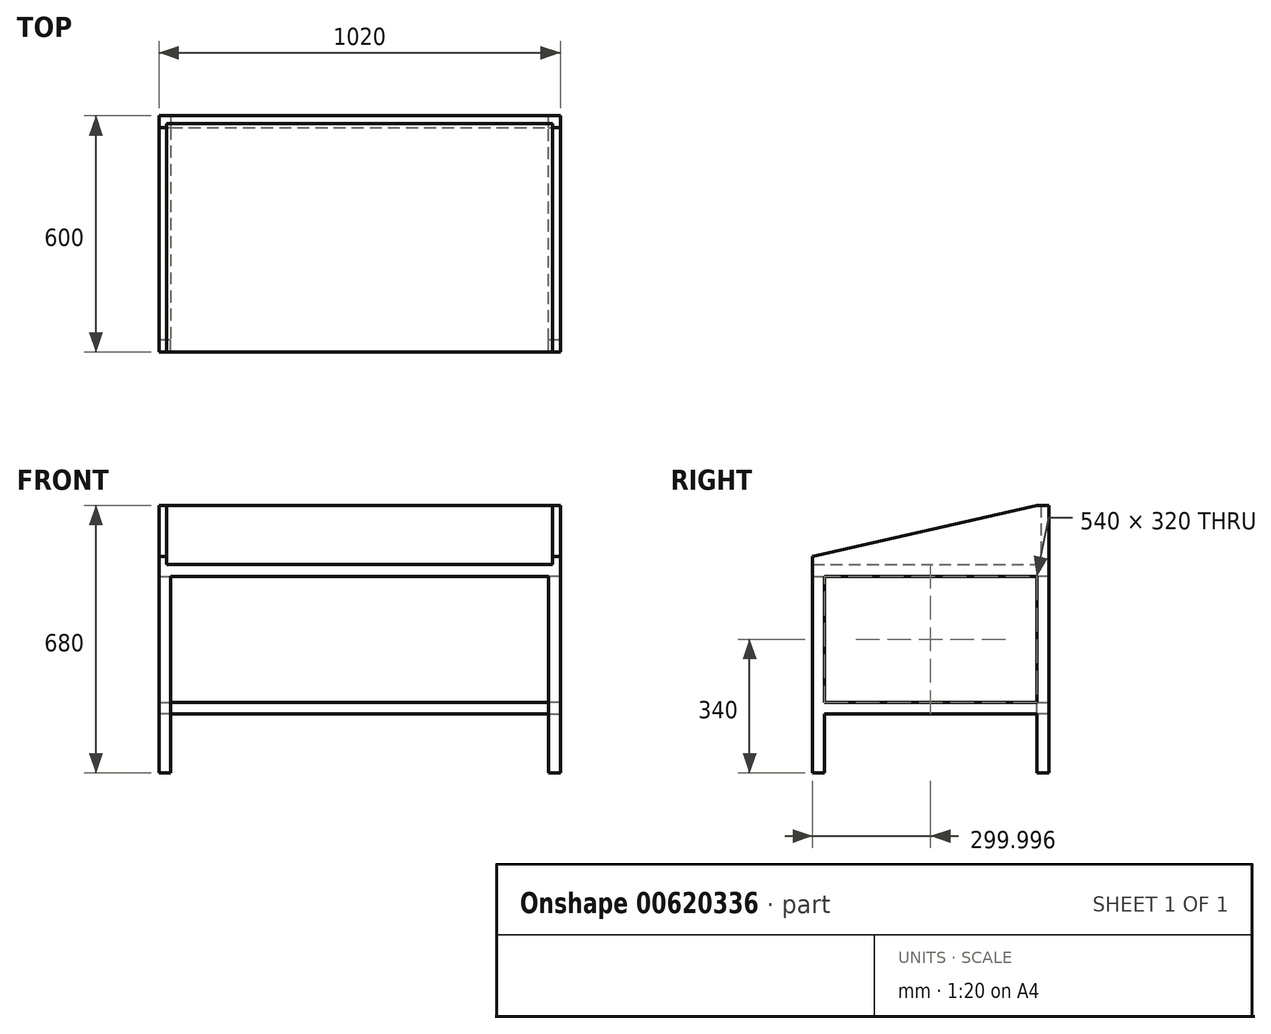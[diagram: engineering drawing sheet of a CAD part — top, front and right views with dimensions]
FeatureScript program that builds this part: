
annotation { "Feature Type Name" : "Feature", "Feature Type Description" : "" }
export const myFeature = defineFeature(function(context is Context, id is Id, definition is map)
    precondition{}
    {
        {
            var Q0;
            Q0=qCreatedBy(makeId("Top.planeOp"),FACE);
            var sketch = newSketch(context, id + "F0", { "sketchPlane" : qUnion([Q0])});
            skLineSegment(sketch, "E0.bottom", {"start": v(-508.02, 248.14) * mm, "end": v(511.98, 248.14) * mm});
            skLineSegment(sketch, "E0.top", {"start": v(-508.02, -351.86) * mm, "end": v(511.98, -351.86) * mm});
            skLineSegment(sketch, "E0.left", {"start": v(-508.02, 248.14) * mm, "end": v(-508.02, -351.86) * mm});
            skLineSegment(sketch, "E0.right", {"start": v(511.98, 248.14) * mm, "end": v(511.98, -351.86) * mm});
            skSolve(sketch);
        }
        {
            var Q0;
            Q0=makeQuery(id+"F0.imprint","IMPRINT",FACE,{"disambiguationData":[TD([[makeQuery(id+"F0.imprint","IMPRINT",EDGE,{"derivedFrom":sQuery(id+"F0.wireOp",EDGE,"E0.bottom")}),-1.0]])]});
            extrude(context, id + "F1", {"entities" : qUnion([Q0]), "depth" : 30 * mm, "offsetDistance" : 25 * mm});
        }
        {
            var Q0;
            Q0=makeQuery(id+"F1.opExtrude","CAP_FACE",FACE,{"disambiguationData":[OSD([sQuery(id+"F0.wireOp",EDGE,"E0.bottom"),sQuery(id+"F0.wireOp",EDGE,"E0.top"),sQuery(id+"F0.wireOp",EDGE,"E0.left"),sQuery(id+"F0.wireOp",EDGE,"E0.right")])],"isStart":false});
            var sketch = newSketch(context, id + "F2", { "sketchPlane" : qUnion([Q0])});
            skLineSegment(sketch, "E1", {"start": v(-508.02, -351.86) * mm, "end": v(-508.02, 248.14) * mm});
            skLineSegment(sketch, "E2", {"start": v(-508.02, 248.14) * mm, "end": v(511.98, 248.14) * mm});
            skLineSegment(sketch, "E3", {"start": v(511.98, 248.14) * mm, "end": v(511.98, -351.86) * mm});
            skLineSegment(sketch, "E4", {"start": v(511.98, -351.86) * mm, "end": v(491.98, -351.86) * mm});
            skLineSegment(sketch, "E5", {"start": v(491.98, -351.86) * mm, "end": v(491.98, 228.14) * mm});
            skLineSegment(sketch, "E6", {"start": v(491.98, 228.14) * mm, "end": v(-488.02, 228.14) * mm});
            skLineSegment(sketch, "E7", {"start": v(-488.02, 228.14) * mm, "end": v(-488.02, -351.86) * mm});
            skLineSegment(sketch, "E8", {"start": v(-488.02, -351.86) * mm, "end": v(-508.02, -351.86) * mm});
            skSolve(sketch);
        }
        {
            var Q0;
            Q0 = qSketchRegion(id + "F2", true);
            extrude(context, id + "F3", {"entities" : qUnion([Q0]), "operationType" : NewBodyOperationType.ADD, "depth" : 150 * mm, "offsetDistance" : 25 * mm});
        }
        {
            var Q0;
            Q0=makeQuery(id+"F3.boolean.opBoolean","MERGE",FACE,{"derivedFrom":[makeQuery(id+"F1.opExtrude","SWEPT_FACE",FACE,{"disambiguationData":[OSD([sQuery(id+"F0.wireOp",EDGE,"E0.left")])]}),makeQuery(id+"F3.opExtrude","SWEPT_FACE",FACE,{"disambiguationData":[OSD([sQuery(id+"F2.wireOp",EDGE,"E1")])]})]});
            var sketch = newSketch(context, id + "F4", { "sketchPlane" : qUnion([Q0])});
            skLineSegment(sketch, "E9", {"start": v(-218.14, 180) * mm, "end": v(351.86, 50) * mm});
            skLineSegment(sketch, "E10", {"start": v(351.86, 50) * mm, "end": v(351.86, 180) * mm});
            skLineSegment(sketch, "E11", {"start": v(351.86, 180) * mm, "end": v(-218.14, 180) * mm});
            skSolve(sketch);
        }
        {
            var Q0;
            Q0=makeQuery(id+"F4.imprint","IMPRINT",FACE,{"disambiguationData":[TD([[makeQuery(id+"F4.imprint","IMPRINT",EDGE,{"derivedFrom":sQuery(id+"F4.wireOp",EDGE,"E9")}),1.0]])]});
            extrude(context, id + "F5", {"entities" : qUnion([Q0]), "operationType" : NewBodyOperationType.REMOVE, "oppositeDirection" : true, "depth" : 2000 * mm, "offsetDistance" : 25 * mm});
        }
        {
            var Q0;
            Q0=makeQuery(id+"F1.opExtrude","CAP_FACE",FACE,{"disambiguationData":[OSD([sQuery(id+"F0.wireOp",EDGE,"E0.bottom"),sQuery(id+"F0.wireOp",EDGE,"E0.top"),sQuery(id+"F0.wireOp",EDGE,"E0.left"),sQuery(id+"F0.wireOp",EDGE,"E0.right")])],"isStart":true});
            var sketch = newSketch(context, id + "F6", { "sketchPlane" : qUnion([Q0])});
            skLineSegment(sketch, "E12.bottom", {"start": v(-508.02, 351.86) * mm, "end": v(-478.02, 351.86) * mm});
            skLineSegment(sketch, "E12.top", {"start": v(-508.02, 321.86) * mm, "end": v(-478.02, 321.86) * mm});
            skLineSegment(sketch, "E12.left", {"start": v(-508.02, 351.86) * mm, "end": v(-508.02, 321.86) * mm});
            skLineSegment(sketch, "E12.right", {"start": v(-478.02, 351.86) * mm, "end": v(-478.02, 321.86) * mm});
            skLineSegment(sketch, "E13.bottom", {"start": v(-508.02, -248.14) * mm, "end": v(-478.02, -248.14) * mm});
            skLineSegment(sketch, "E13.top", {"start": v(-508.02, -218.14) * mm, "end": v(-478.02, -218.14) * mm});
            skLineSegment(sketch, "E13.left", {"start": v(-508.02, -248.14) * mm, "end": v(-508.02, -218.14) * mm});
            skLineSegment(sketch, "E13.right", {"start": v(-478.02, -248.14) * mm, "end": v(-478.02, -218.14) * mm});
            skLineSegment(sketch, "E14.bottom", {"start": v(511.98, 351.86) * mm, "end": v(481.98, 351.86) * mm});
            skLineSegment(sketch, "E14.top", {"start": v(511.98, 321.86) * mm, "end": v(481.98, 321.86) * mm});
            skLineSegment(sketch, "E14.left", {"start": v(511.98, 351.86) * mm, "end": v(511.98, 321.86) * mm});
            skLineSegment(sketch, "E14.right", {"start": v(481.98, 351.86) * mm, "end": v(481.98, 321.86) * mm});
            skLineSegment(sketch, "E15.bottom", {"start": v(511.98, -248.14) * mm, "end": v(481.98, -248.14) * mm});
            skLineSegment(sketch, "E15.top", {"start": v(511.98, -218.14) * mm, "end": v(481.98, -218.14) * mm});
            skLineSegment(sketch, "E15.left", {"start": v(511.98, -248.14) * mm, "end": v(511.98, -218.14) * mm});
            skLineSegment(sketch, "E15.right", {"start": v(481.98, -248.14) * mm, "end": v(481.98, -218.14) * mm});
            skSolve(sketch);
        }
        {
            var Q0;
            Q0 = qSketchRegion(id + "F6", true);
            extrude(context, id + "F7", {"entities" : qUnion([Q0]), "operationType" : NewBodyOperationType.ADD, "depth" : 500 * mm, "offsetDistance" : 25 * mm});
        }
        {
            var Q0;
            Q0=makeQuery(id+"F7.opExtrude","SWEPT_FACE",FACE,{"disambiguationData":[OSD([sQuery(id+"F6.wireOp",EDGE,"E12.top")])]});
            var sketch = newSketch(context, id + "F8", { "sketchPlane" : qUnion([Q0])});
            skLineSegment(sketch, "E16.bottom", {"start": v(478.02, -320) * mm, "end": v(508.02, -320) * mm});
            skLineSegment(sketch, "E16.top", {"start": v(478.02, -350) * mm, "end": v(508.02, -350) * mm});
            skLineSegment(sketch, "E16.left", {"start": v(478.02, -320) * mm, "end": v(478.02, -350) * mm});
            skLineSegment(sketch, "E16.right", {"start": v(508.02, -320) * mm, "end": v(508.02, -350) * mm});
            skSolve(sketch);
        }
        {
            var Q0;
            Q0 = qSketchRegion(id + "F8", true);
            extrude(context, id + "F9", {"entities" : qUnion([Q0]), "operationType" : NewBodyOperationType.ADD, "endBound" : BoundingType.UP_TO_NEXT, "depth" : 25 * mm, "offsetDistance" : 25 * mm});
        }
        {
            var Q0;
            Q0=makeQuery(id+"F7.opExtrude","SWEPT_FACE",FACE,{"disambiguationData":[OSD([sQuery(id+"F6.wireOp",EDGE,"E15.top")])]});
            var sketch = newSketch(context, id + "F10", { "sketchPlane" : qUnion([Q0])});
            skLineSegment(sketch, "E17.bottom", {"start": v(481.98, -320) * mm, "end": v(511.98, -320) * mm});
            skLineSegment(sketch, "E17.top", {"start": v(481.98, -350) * mm, "end": v(511.98, -350) * mm});
            skLineSegment(sketch, "E17.left", {"start": v(481.98, -320) * mm, "end": v(481.98, -350) * mm});
            skLineSegment(sketch, "E17.right", {"start": v(511.98, -320) * mm, "end": v(511.98, -350) * mm});
            skSolve(sketch);
        }
        {
            var Q0;
            Q0 = qSketchRegion(id + "F10", true);
            extrude(context, id + "F11", {"entities" : qUnion([Q0]), "operationType" : NewBodyOperationType.ADD, "endBound" : BoundingType.UP_TO_NEXT, "depth" : 25 * mm, "offsetDistance" : 25 * mm});
        }
        {
            var Q0;
            Q0=makeQuery(id+"F11.boolean.opBoolean","MERGE",FACE,{"derivedFrom":[makeQuery(id+"F7.opExtrude","SWEPT_FACE",FACE,{"disambiguationData":[OSD([sQuery(id+"F6.wireOp",EDGE,"E14.right")])]}),makeQuery(id+"F7.opExtrude","SWEPT_FACE",FACE,{"disambiguationData":[OSD([sQuery(id+"F6.wireOp",EDGE,"E15.right")])]}),makeQuery(id+"F11.opExtrude","SWEPT_FACE",FACE,{"disambiguationData":[OSD([sQuery(id+"F10.wireOp",EDGE,"E17.left")])]})]});
            var sketch = newSketch(context, id + "F12", { "sketchPlane" : qUnion([Q0])});
            skLineSegment(sketch, "E18.bottom", {"start": v(-218.14, -320) * mm, "end": v(-248.14, -320) * mm});
            skLineSegment(sketch, "E18.top", {"start": v(-218.14, -350) * mm, "end": v(-248.14, -350) * mm});
            skLineSegment(sketch, "E18.left", {"start": v(-218.14, -320) * mm, "end": v(-218.14, -350) * mm});
            skLineSegment(sketch, "E18.right", {"start": v(-248.14, -320) * mm, "end": v(-248.14, -350) * mm});
            skSolve(sketch);
        }
        {
            var Q0;
            Q0 = qSketchRegion(id + "F12", true);
            extrude(context, id + "F13", {"entities" : qUnion([Q0]), "operationType" : NewBodyOperationType.ADD, "endBound" : BoundingType.UP_TO_NEXT, "depth" : 25 * mm, "offsetDistance" : 25 * mm});
        }
    });
